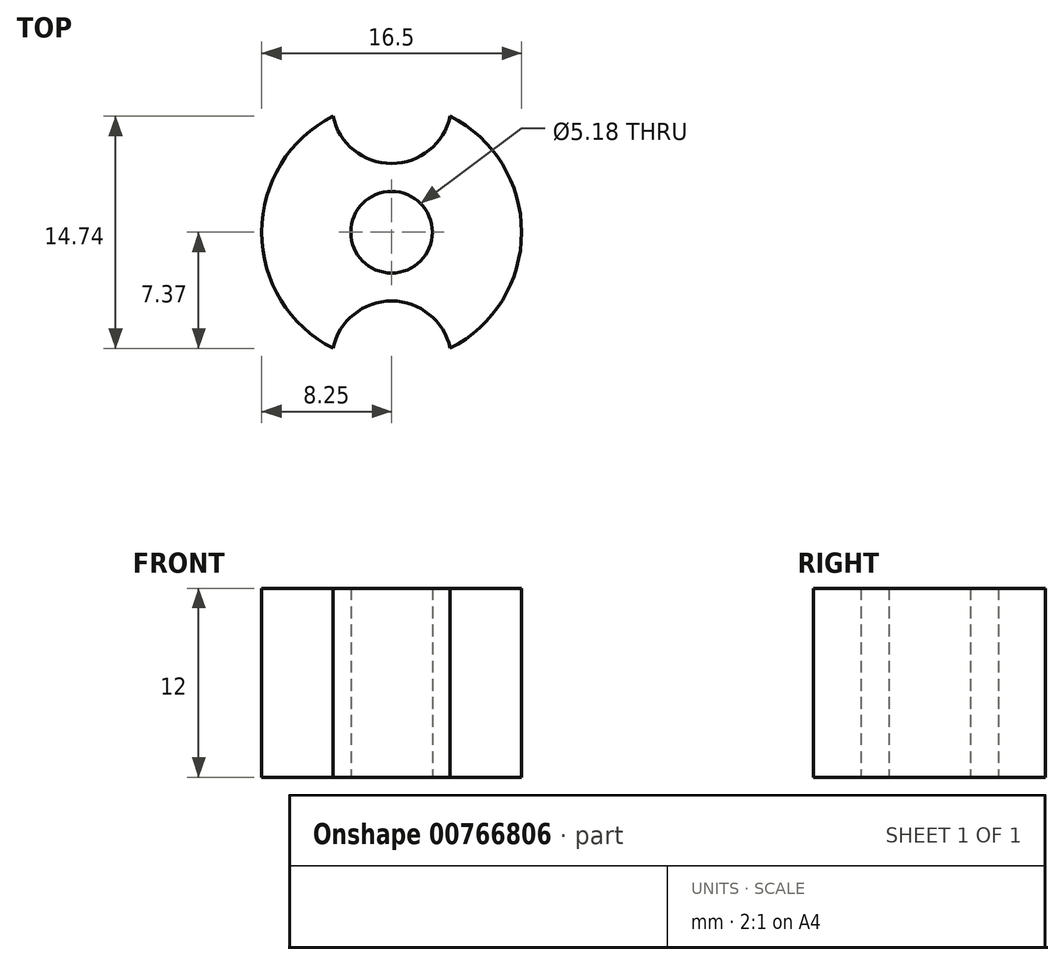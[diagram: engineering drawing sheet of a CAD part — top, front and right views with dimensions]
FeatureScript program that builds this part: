
annotation { "Feature Type Name" : "Feature", "Feature Type Description" : "" }
export const myFeature = defineFeature(function(context is Context, id is Id, definition is map)
    precondition{}
    {
        {
            var Q0;
            Q0=qCreatedBy(makeId("Top.planeOp"),FACE);
            var sketch = newSketch(context, id + "F0", { "sketchPlane" : qUnion([Q0])});
            skArc(sketch, "E0", {"start": v(-3.72, 7.37) * mm, "mid": v(-8.26, 0) * mm, "end": v(-3.72, -7.37) * mm});
            skArc(sketch, "E1", {"start": v(-3.72, 7.37) * mm, "mid": v(0, 4.37) * mm, "end": v(3.72, 7.37) * mm});
            skArc(sketch, "E2.MirrorCS", {"start": v(-3.72, -7.37) * mm, "mid": v(0, -4.37) * mm, "end": v(3.72, -7.37) * mm});
            skArc(sketch, "E3.trimOffspring", {"start": v(3.72, -7.37) * mm, "mid": v(8.26, 0) * mm, "end": v(3.72, 7.37) * mm});
            skCircle(sketch, "E4", {"center": v(0, 0) * mm, "radius": 2.6 * mm});
            skSolve(sketch);
        }
        {
            var Q0;
            Q0=makeQuery(id+"F0.imprint","IMPRINT",FACE,{"disambiguationData":[TD([[makeQuery(id+"F0.imprint","IMPRINT",EDGE,{"derivedFrom":sQuery(id+"F0.wireOp",EDGE,"E0")}),1.0]])]});
            extrude(context, id + "F1", {"entities" : qUnion([Q0]), "depth" : 12 * mm, "offsetDistance" : 25.4 * mm});
        }
    });
